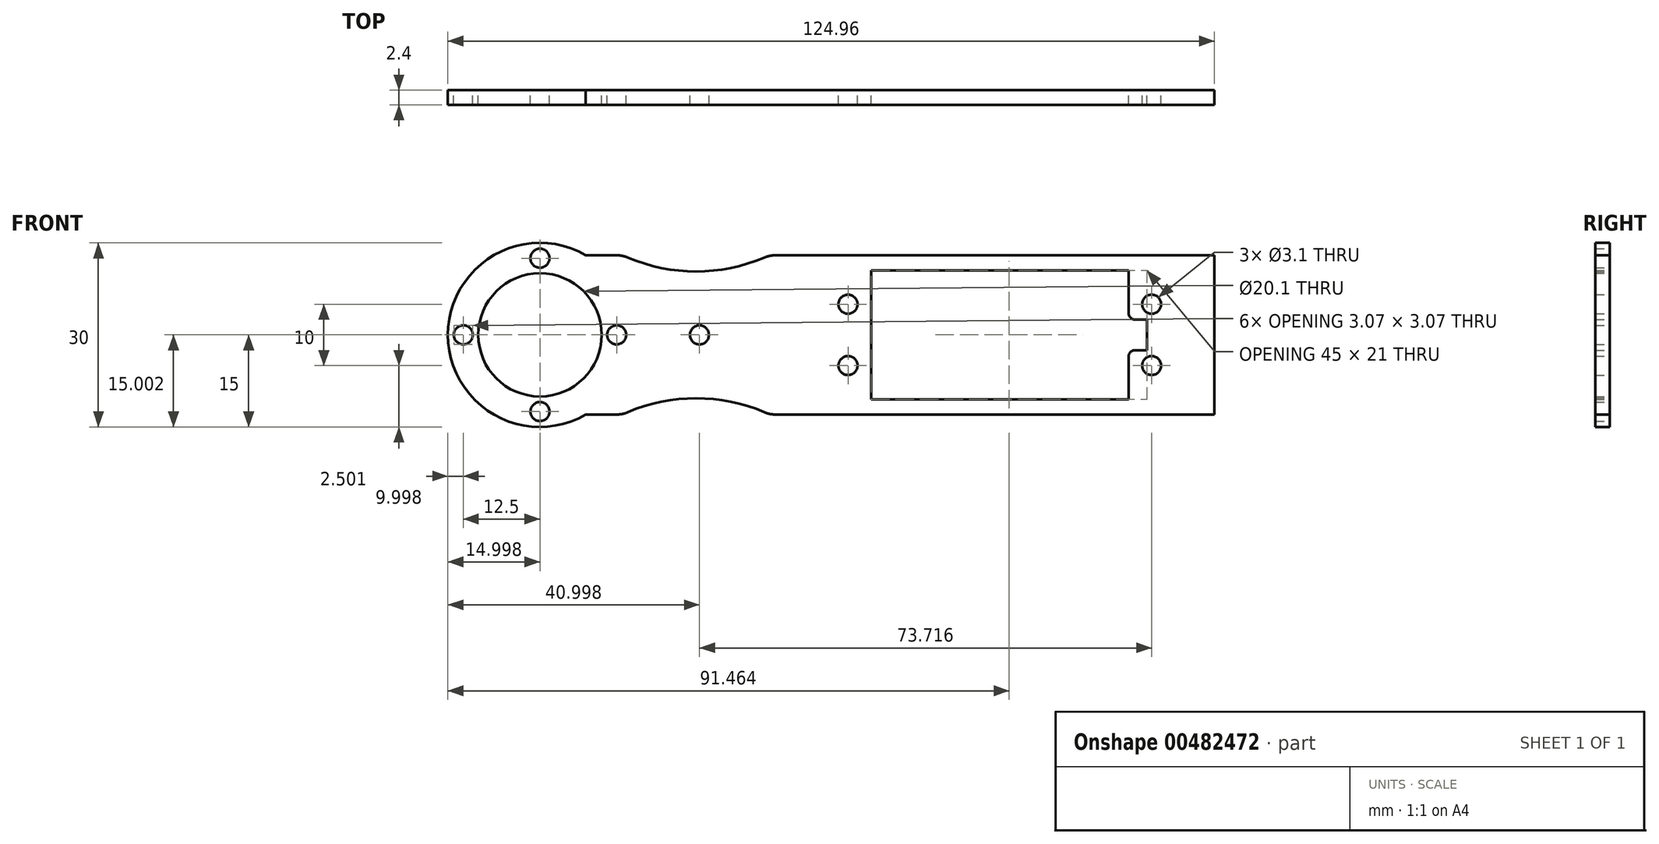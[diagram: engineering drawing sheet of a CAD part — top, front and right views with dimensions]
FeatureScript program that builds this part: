
annotation { "Feature Type Name" : "Feature", "Feature Type Description" : "" }
export const myFeature = defineFeature(function(context is Context, id is Id, definition is map)
    precondition{}
    {
        {
            var Q0;
            Q0=qCreatedBy(makeId("Front.planeOp"),FACE);
            var sketch = newSketch(context, id + "F0", { "sketchPlane" : qUnion([Q0])});
            skCircle(sketch, "E0", {"center": v(-113.5, 36.93) * mm, "radius": 1.55 * mm});
            skCircle(sketch, "E1", {"center": v(-113.5, 26.93) * mm, "radius": 1.55 * mm});
            skCircle(sketch, "E2", {"center": v(-64, 36.93) * mm, "radius": 1.55 * mm});
            skCircle(sketch, "E3", {"center": v(-64, 26.93) * mm, "radius": 1.55 * mm});
            skLineSegment(sketch, "E4.bottom", {"start": v(-109.75, 42.43) * mm, "end": v(-67.75, 42.43) * mm});
            skLineSegment(sketch, "E4.top", {"start": v(-109.75, 21.43) * mm, "end": v(-67.75, 21.43) * mm});
            skLineSegment(sketch, "E4.right", {"start": v(-67.75, 42.43) * mm, "end": v(-67.75, 34.43) * mm});
            skLineSegment(sketch, "E5", {"start": v(-53.75, 44.93) * mm, "end": v(-53.75, 18.93) * mm});
            skLineSegment(sketch, "E6", {"start": v(-123.75, 44.93) * mm, "end": v(-123.75, 18.93) * mm});
            skLineSegment(sketch, "E7", {"start": v(-53.75, 44.93) * mm, "end": v(-125.17, 44.93) * mm});
            skLineSegment(sketch, "E8", {"start": v(-53.75, 18.93) * mm, "end": v(-125.17, 18.93) * mm});
            skCircle(sketch, "E9", {"center": v(-163.71, 31.93) * mm, "radius": 10.05 * mm});
            skArc(sketch, "E10", {"start": v(-156.23, 44.93) * mm, "mid": v(-178.71, 31.93) * mm, "end": v(-156.23, 18.93) * mm});
            skLineSegment(sketch, "E11", {"start": v(-67.75, 34.43) * mm, "end": v(-64.75, 34.43) * mm});
            skLineSegment(sketch, "E12", {"start": v(-64.75, 34.43) * mm, "end": v(-64.75, 29.43) * mm});
            skLineSegment(sketch, "E13", {"start": v(-64.75, 29.43) * mm, "end": v(-67.75, 29.43) * mm});
            skLineSegment(sketch, "E14.trimOffspring", {"start": v(-67.75, 29.43) * mm, "end": v(-67.75, 21.43) * mm});
            skLineSegment(sketch, "E15", {"start": v(-109.75, 42.43) * mm, "end": v(-109.75, 21.43) * mm});
            skLineSegment(sketch, "E16", {"start": v(-163.71, 31.93) * mm, "end": v(-163.71, 53.74) * mm, "construction": true});
            skLineSegment(sketch, "E17", {"start": v(-163.71, 53.74) * mm, "end": v(-163.71, 11.81) * mm, "construction": true});
            skLineSegment(sketch, "E18", {"start": v(-187.92, 31.93) * mm, "end": v(-147.13, 31.93) * mm, "construction": true});
            skPoint(sketch, "E18.endSnap0", {"position": v(-178.71, 31.93) * mm});
            skCircle(sketch, "E19", {"center": v(-163.71, 31.93) * mm, "radius": 12.5 * mm, "construction": true});
            skCircle(sketch, "E20", {"center": v(-163.71, 44.43) * mm, "radius": 1.55 * mm});
            skCircle(sketch, "E21", {"center": v(-176.21, 31.93) * mm, "radius": 1.55 * mm});
            skCircle(sketch, "E22", {"center": v(-151.21, 31.93) * mm, "radius": 1.55 * mm});
            skCircle(sketch, "E23", {"center": v(-163.71, 19.43) * mm, "radius": 1.55 * mm});
            skCircle(sketch, "E24", {"center": v(-113.49, 36.93) * mm, "radius": 1.55 * mm});
            skCircle(sketch, "E25", {"center": v(-113.49, 26.93) * mm, "radius": 1.55 * mm});
            skCircle(sketch, "E26", {"center": v(-163.7, 44.43) * mm, "radius": 1.55 * mm});
            skCircle(sketch, "E27", {"center": v(-176.2, 31.93) * mm, "radius": 1.55 * mm});
            skCircle(sketch, "E28", {"center": v(-151.2, 31.93) * mm, "radius": 1.55 * mm});
            skCircle(sketch, "E29", {"center": v(-163.7, 19.43) * mm, "radius": 1.55 * mm});
            skArc(sketch, "E30", {"start": v(-149.4, 44.53) * mm, "mid": v(-138.26, 42.27) * mm, "end": v(-127.13, 44.53) * mm});
            skArc(sketch, "E31.filletArc", {"start": v(-125.17, 44.93) * mm, "mid": v(-126.17, 44.83) * mm, "end": v(-127.13, 44.53) * mm});
            skArc(sketch, "E32.filletArc", {"start": v(-149.4, 44.53) * mm, "mid": v(-150.35, 44.83) * mm, "end": v(-151.35, 44.93) * mm});
            skArc(sketch, "E33.MirrorCS", {"start": v(-149.4, 19.33) * mm, "mid": v(-138.26, 21.6) * mm, "end": v(-127.13, 19.33) * mm});
            skArc(sketch, "E34.MirrorCS", {"start": v(-125.17, 18.93) * mm, "mid": v(-126.17, 19.03) * mm, "end": v(-127.13, 19.33) * mm});
            skArc(sketch, "E35.MirrorCS", {"start": v(-149.4, 19.33) * mm, "mid": v(-150.35, 19.03) * mm, "end": v(-151.35, 18.93) * mm});
            skLineSegment(sketch, "E36.trimOffspring", {"start": v(-151.35, 18.93) * mm, "end": v(-156.23, 18.93) * mm});
            skLineSegment(sketch, "E37.trimOffspring", {"start": v(-151.35, 44.93) * mm, "end": v(-156.23, 44.93) * mm});
            skLineSegment(sketch, "E38", {"start": v(-183.5, 31.93) * mm, "end": v(-111.93, 31.93) * mm, "construction": true});
            skPoint(sketch, "E38.endSnap0", {"position": v(-123.75, 31.93) * mm});
            skCircle(sketch, "E39", {"center": v(-137.71, 31.93) * mm, "radius": 1.55 * mm});
            skSolve(sketch);
        }
        {
            var Q0;
            Q0 = qSketchRegion(id + "F0", true);
            extrude(context, id + "F1", {"entities" : qUnion([Q0]), "depth" : 2.4 * mm, "offsetDistance" : 25 * mm});
        }
        {
            var Q0;
            Q0=makeQuery(id+"F1.opExtrude","SWEPT_EDGE",EDGE,{"disambiguationData":[OSD([sQuery(id+"F0.wireOp",EDGE,"E4.right"),sQuery(id+"F0.wireOp",EDGE,"E11")])]});
            var Q1;
            Q1=makeQuery(id+"F1.opExtrude","SWEPT_EDGE",EDGE,{"disambiguationData":[OSD([sQuery(id+"F0.wireOp",EDGE,"E13"),sQuery(id+"F0.wireOp",EDGE,"E14.trimOffspring")])]});
            fillet(context, id + "F2", {"entities" : qUnion([Q0, Q1]), "radius" : 1 * mm, "tangentPropagation" : true, "allowEdgeOverflow" : false});
        }
    });
